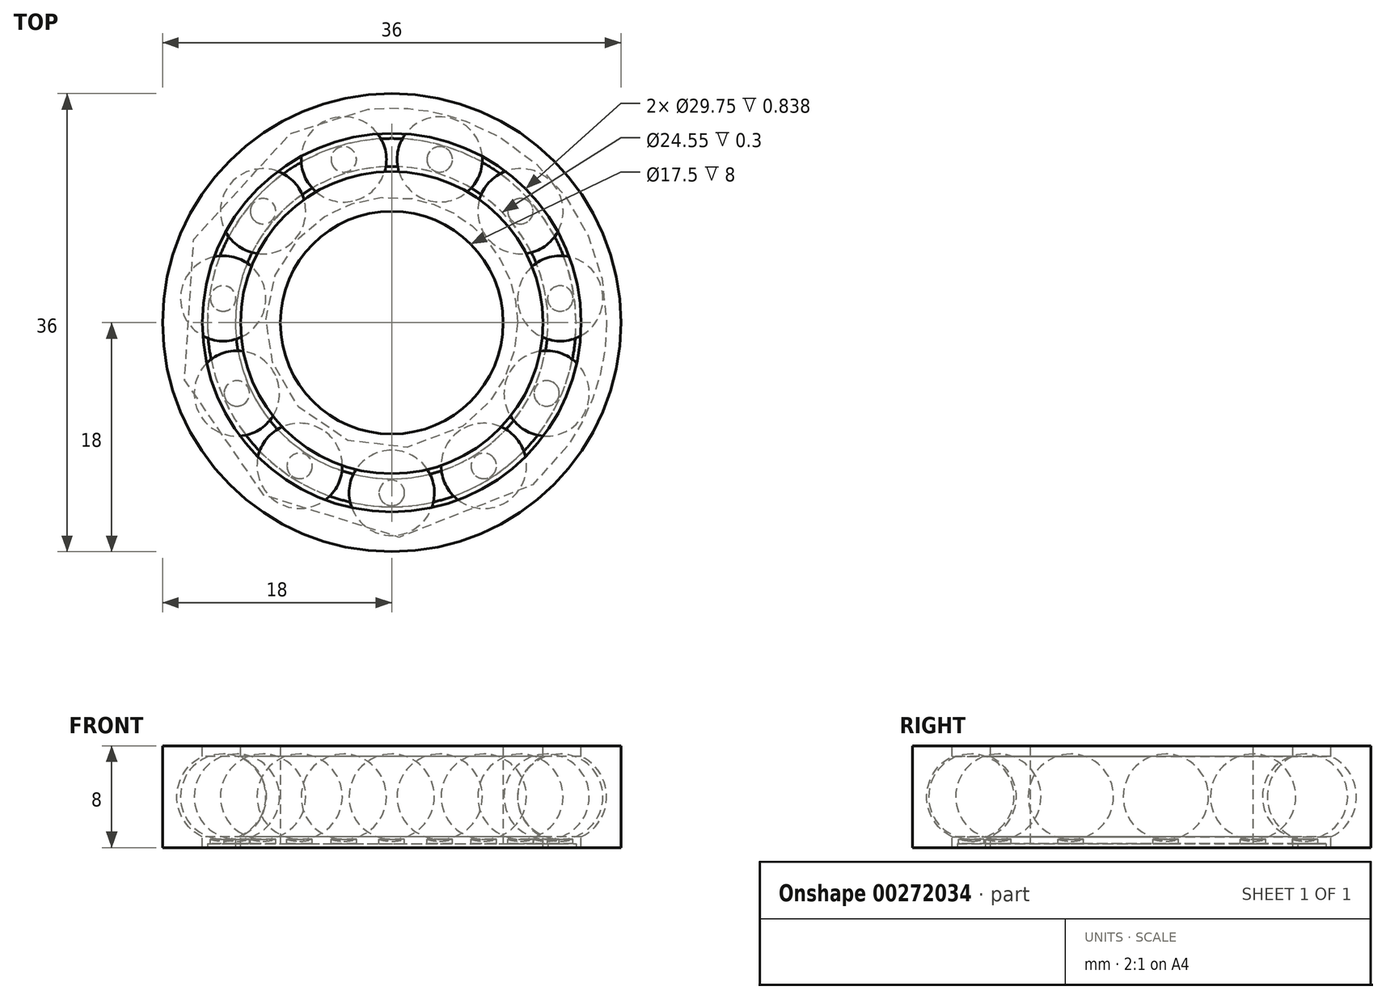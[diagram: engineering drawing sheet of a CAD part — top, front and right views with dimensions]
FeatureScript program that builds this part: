
annotation { "Feature Type Name" : "Feature", "Feature Type Description" : "" }
export const myFeature = defineFeature(function(context is Context, id is Id, definition is map)
    precondition{}
    {
        {
            var Q0;
            Q0=qCreatedBy(makeId("Top.planeOp"),FACE);
            var sketch = newSketch(context, id + "F0", { "sketchPlane" : qUnion([Q0])});
            skCircle(sketch, "E0", {"center": v(0, 0) * mm, "radius": 8.75 * mm});
            skCircle(sketch, "E1", {"center": v(0, 0) * mm, "radius": 18 * mm});
            skSolve(sketch);
        }
        {
            var Q0;
            Q0=makeQuery(id+"F0.imprint","IMPRINT",FACE,{"disambiguationData":[TD([[makeQuery(id+"F0.imprint","IMPRINT",EDGE,{"derivedFrom":sQuery(id+"F0.wireOp",EDGE,"E0")}),-1.0]])]});
            extrude(context, id + "F1", {"entities" : qUnion([Q0]), "depth" : 8 * mm});
        }
        {
            var Q0;
            Q0=qCreatedBy(makeId("Right.planeOp"),FACE);
            var sketch = newSketch(context, id + "F2", { "sketchPlane" : qUnion([Q0])});
            skLineSegment(sketch, "E2.0", {"start": v(-18, 8) * mm, "end": v(-8.75, 8) * mm});
            skCircle(sketch, "E3", {"center": v(-13.38, 4) * mm, "radius": 3.5 * mm});
            skPoint(sketch, "E4.0.start.orphan", {"position": v(-8.75, 8) * mm});
            skPoint(sketch, "E5", {"position": v(-13.38, 8) * mm});
            skLineSegment(sketch, "E6", {"start": v(-13.38, 8) * mm, "end": v(-13.38, 0) * mm});
            skLineSegment(sketch, "E7", {"start": v(-14.88, 7.16) * mm, "end": v(-14.88, 8) * mm});
            skLineSegment(sketch, "E8", {"start": v(-11.88, 7.16) * mm, "end": v(-11.88, 8) * mm});
            skLineSegment(sketch, "E9", {"start": v(-14.88, 0.84) * mm, "end": v(-14.88, 0) * mm});
            skLineSegment(sketch, "E10", {"start": v(-11.88, 0.84) * mm, "end": v(-11.88, 0) * mm});
            skLineSegment(sketch, "E11", {"start": v(-14.88, 0) * mm, "end": v(-11.88, 0) * mm});
            skSolve(sketch);
        }
        {
            var Q0;
            Q0 = qSketchRegion(id + "F2", true);
            var Q1;
            Q1=makeQuery(id+"F1.opExtrude","CAP_EDGE",EDGE,{"disambiguationData":[OSD([sQuery(id+"F0.wireOp",EDGE,"E1")])],"isStart":false});
            revolve(context, id + "F3", {"operationType" : NewBodyOperationType.REMOVE, "entities" : qUnion([Q0]), "axis" : qUnion([Q1]), "revolveType" : RevolveType.FULL, "oppositeDirection" : true});
        }
        {
            var Q0;
            Q0=qCreatedBy(makeId("Right.planeOp"),FACE);
            var sketch = newSketch(context, id + "F4", { "sketchPlane" : qUnion([Q0])});
            skArc(sketch, "E12", {"start": v(-13.38, 7.35) * mm, "mid": v(-16.73, 4) * mm, "end": v(-13.38, 0.65) * mm});
            skLineSegment(sketch, "E13", {"start": v(-13.38, 7.35) * mm, "end": v(-13.38, 0.65) * mm});
            skLineSegment(sketch, "E14", {"start": v(-14.38, 0.65) * mm, "end": v(-14.38, 0) * mm});
            skLineSegment(sketch, "E15", {"start": v(-14.38, 0) * mm, "end": v(-13.38, 0) * mm});
            skLineSegment(sketch, "E16", {"start": v(-13.38, 0) * mm, "end": v(-13.38, 0.5) * mm});
            skArc(sketch, "E17", {"start": v(-14.38, 0.65) * mm, "mid": v(-13.88, 0.54) * mm, "end": v(-13.38, 0.5) * mm});
            skSolve(sketch);
        }
        {
            var Q0;
            Q0=makeQuery(id+"F4.imprint","IMPRINT",FACE,{"disambiguationData":[TD([[makeQuery(id+"F4.imprint","IMPRINT",EDGE,{"derivedFrom":sQuery(id+"F4.wireOp",EDGE,"E12")}),1.0]])]});
            var Q1;
            Q1=makeQuery(id+"F4.imprint","IMPRINT",FACE,{"disambiguationData":[TD([[makeQuery(id+"F4.imprint","IMPRINT",EDGE,{"derivedFrom":sQuery(id+"F4.wireOp",EDGE,"E14")}),1.0]])]});
            var Q2;
            Q2=sQuery(id+"F4.wireOp",EDGE,"E13");
            revolve(context, id + "F5", {"entities" : qUnion([Q0, Q1]), "axis" : qUnion([Q2]), "revolveType" : RevolveType.FULL});
        }
        {
            var Q0;
            Q0=makeQuery(id+"F5.opRevolve","SWEPT_BODY",BODY,{"disambiguationData":[OSD([sQuery(id+"F4.wireOp",EDGE,"E12"),sQuery(id+"F4.wireOp",EDGE,"E13")])]});
            var Q1;
            Q1=makeQuery(id+"F5.opRevolve","SWEPT_BODY",BODY,{"disambiguationData":[OSD([sQuery(id+"F4.wireOp",EDGE,"E14"),sQuery(id+"F4.wireOp",EDGE,"E15"),sQuery(id+"F4.wireOp",EDGE,"E16"),sQuery(id+"F4.wireOp",EDGE,"E17")])]});
            var Q2;
            Q2=makeQuery(id+"F3.boolean.opBoolean","COPY",EDGE,{"derivedFrom":makeQuery(id+"F3.opRevolve","SWEPT_EDGE",EDGE,{"disambiguationData":[OSD([sQuery(id+"F2.wireOp",EDGE,"E10"),sQuery(id+"F2.wireOp",EDGE,"E11")])]})});
            circularPattern(context, id + "F6", {"entities" : qUnion([Q0, Q1]), "axis" : qUnion([Q2]), "angle" : 360 * degree, "instanceCount" : 11, "equalSpace" : true});
        }
        {
            var Q0;
            Q0=qCreatedBy(makeId("Right.planeOp"),FACE);
            var sketch = newSketch(context, id + "F7", { "sketchPlane" : qUnion([Q0])});
            skLineSegment(sketch, "E18.bottom", {"start": v(-12.28, 0) * mm, "end": v(-14.48, 0) * mm});
            skLineSegment(sketch, "E18.top", {"start": v(-12.28, 0.3) * mm, "end": v(-14.48, 0.3) * mm});
            skLineSegment(sketch, "E18.left", {"start": v(-12.28, 0) * mm, "end": v(-12.28, 0.3) * mm});
            skLineSegment(sketch, "E18.right", {"start": v(-14.47, 0) * mm, "end": v(-14.47, 0.3) * mm});
            skSolve(sketch);
        }
        {
            var Q0;
            Q0 = qSketchRegion(id + "F7", true);
            var Q1;
            Q1=makeQuery(id+"F3.boolean.opBoolean","COPY",EDGE,{"derivedFrom":makeQuery(id+"F3.opRevolve","SWEPT_EDGE",EDGE,{"disambiguationData":[OSD([sQuery(id+"F2.wireOp",EDGE,"E10"),sQuery(id+"F2.wireOp",EDGE,"E11")])]})});
            revolve(context, id + "F8", {"operationType" : NewBodyOperationType.ADD, "entities" : qUnion([Q0]), "axis" : qUnion([Q1]), "revolveType" : RevolveType.FULL});
        }
    });
